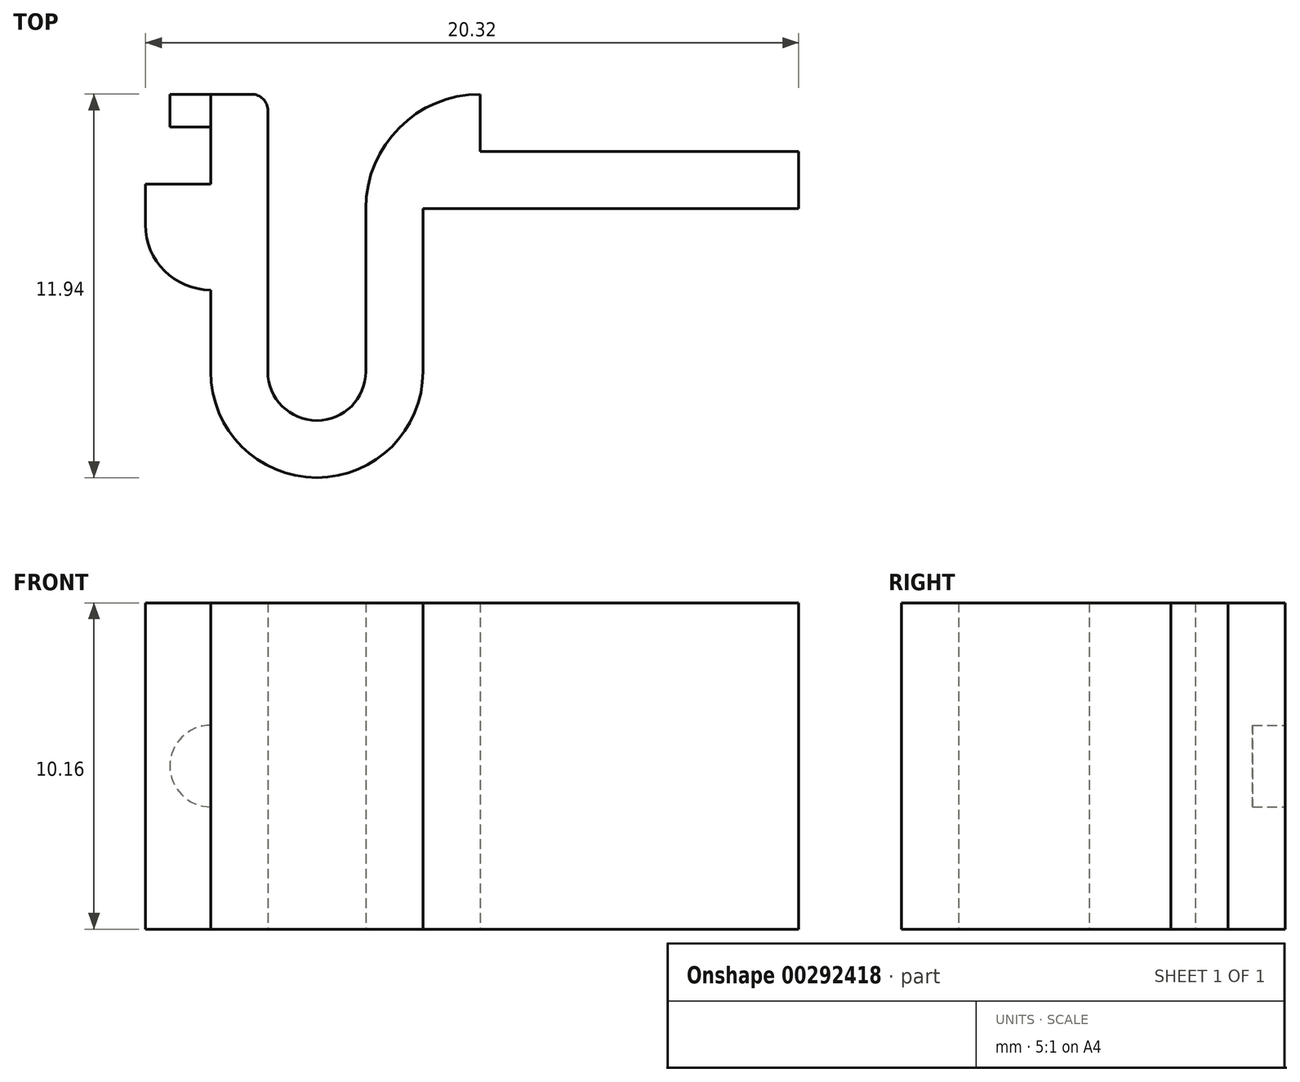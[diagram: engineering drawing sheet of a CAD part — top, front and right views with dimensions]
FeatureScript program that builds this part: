
annotation { "Feature Type Name" : "Feature", "Feature Type Description" : "" }
export const myFeature = defineFeature(function(context is Context, id is Id, definition is map)
    precondition{}
    {
        {
            var Q0;
            Q0=qCreatedBy(makeId("Top.planeOp"),FACE);
            var sketch = newSketch(context, id + "F0", { "sketchPlane" : qUnion([Q0])});
            skLineSegment(sketch, "E0.bottom", {"start": v(-3.3, 5.08) * mm, "end": v(-1.52, 5.08) * mm});
            skLineSegment(sketch, "E0.top", {"start": v(-3.3, 0) * mm, "end": v(-1.52, 0) * mm});
            skLineSegment(sketch, "E0.left", {"start": v(-3.3, 5.08) * mm, "end": v(-3.3, 0) * mm});
            skLineSegment(sketch, "E0.right", {"start": v(3.3, 5.08) * mm, "end": v(3.3, 0) * mm});
            skPoint(sketch, "E1", {"position": v(0, 0) * mm});
            skArc(sketch, "E2", {"start": v(-3.3, 0) * mm, "mid": v(0, -3.3) * mm, "end": v(3.3, 0) * mm});
            skLineSegment(sketch, "E3.0", {"start": v(1.52, 5.08) * mm, "end": v(1.52, 0) * mm});
            skArc(sketch, "E3.1", {"start": v(-1.52, 0) * mm, "mid": v(0, -1.52) * mm, "end": v(1.52, 0) * mm});
            skLineSegment(sketch, "E3.2", {"start": v(-1.52, 5.08) * mm, "end": v(-1.52, 0) * mm});
            skLineSegment(sketch, "E4.trimOffspring", {"start": v(1.52, 5.08) * mm, "end": v(3.3, 5.08) * mm});
            skLineSegment(sketch, "E5.trimOffspring", {"start": v(1.52, 0) * mm, "end": v(3.3, 0) * mm});
            skArc(sketch, "E6", {"start": v(5.08, 6.86) * mm, "mid": v(3.82, 6.34) * mm, "end": v(3.3, 5.08) * mm});
            skArc(sketch, "E7", {"start": v(5.08, 8.64) * mm, "mid": v(2.57, 7.6) * mm, "end": v(1.52, 5.08) * mm});
            skLineSegment(sketch, "E8", {"start": v(5.08, 8.64) * mm, "end": v(5.08, 6.86) * mm});
            skPoint(sketch, "E9", {"position": v(-3.3, 4.57) * mm});
            skLineSegment(sketch, "E10.top", {"start": v(-3.3, 8.64) * mm, "end": v(-1.52, 8.64) * mm});
            skLineSegment(sketch, "E10.left", {"start": v(-3.3, 5.08) * mm, "end": v(-3.3, 8.64) * mm});
            skLineSegment(sketch, "E10.right", {"start": v(-1.52, 5.08) * mm, "end": v(-1.52, 8.64) * mm});
            skPoint(sketch, "E11", {"position": v(-3.3, 5.84) * mm});
            skArc(sketch, "E12", {"start": v(-5.33, 4.57) * mm, "mid": v(-4.74, 3.14) * mm, "end": v(-3.3, 2.54) * mm});
            skLineSegment(sketch, "E13.bottom", {"start": v(-5.33, 4.57) * mm, "end": v(-3.3, 4.57) * mm});
            skLineSegment(sketch, "E13.top", {"start": v(-5.33, 5.84) * mm, "end": v(-3.3, 5.84) * mm});
            skLineSegment(sketch, "E13.left", {"start": v(-5.33, 4.57) * mm, "end": v(-5.33, 5.84) * mm});
            skLineSegment(sketch, "E13.right", {"start": v(-3.3, 4.57) * mm, "end": v(-3.3, 5.84) * mm});
            skLineSegment(sketch, "E14.bottom", {"start": v(3.3, 5.08) * mm, "end": v(14.99, 5.08) * mm});
            skLineSegment(sketch, "E14.top", {"start": v(5.08, 6.86) * mm, "end": v(14.99, 6.86) * mm});
            skLineSegment(sketch, "E14.right", {"start": v(14.99, 5.08) * mm, "end": v(14.99, 6.86) * mm});
            skSolve(sketch);
        }
        {
            var Q0;
            Q0 = qSketchRegion(id + "F0", true);
            extrude(context, id + "F1", {"entities" : qUnion([Q0]), "depth" : 10.16 * mm});
        }
        {
            var Q0;
            Q0=makeQuery(id+"F1.opExtrude","SWEPT_FACE",FACE,{"disambiguationData":[OSD([sQuery(id+"F0.wireOp",EDGE,"E10.top")])]});
            var sketch = newSketch(context, id + "F2", { "sketchPlane" : qUnion([Q0])});
            skArc(sketch, "E15", {"start": v(3.3, 3.81) * mm, "mid": v(4.57, 5.08) * mm, "end": v(3.3, 6.35) * mm});
            skSolve(sketch);
        }
        {
            var Q0;
            {var subQ0=sQuery(id+"F2.wireOp",EDGE,"E15");Q0=makeQuery(id+"F2.imprint","IMPRINT",FACE,{"disambiguationData":[TD([[makeQuery(id+"F2.imprint","IMPRINT",EDGE,{"derivedFrom":subQ0}),1.0]])]});}
            extrude(context, id + "F3", {"entities" : qUnion([Q0]), "operationType" : NewBodyOperationType.ADD, "oppositeDirection" : true, "depth" : 1.02 * mm});
        }
        {
            var Q0;
            Q0=makeQuery(id+"F1.opExtrude","SWEPT_EDGE",EDGE,{"disambiguationData":[OSD([sQuery(id+"F0.wireOp",EDGE,"E10.top"),sQuery(id+"F0.wireOp",EDGE,"E10.right")])]});
            fillet(context, id + "F4", {"entities" : qUnion([Q0]), "radius" : 0.5 * mm, "tangentPropagation" : true, "allowEdgeOverflow" : false});
        }
    });
